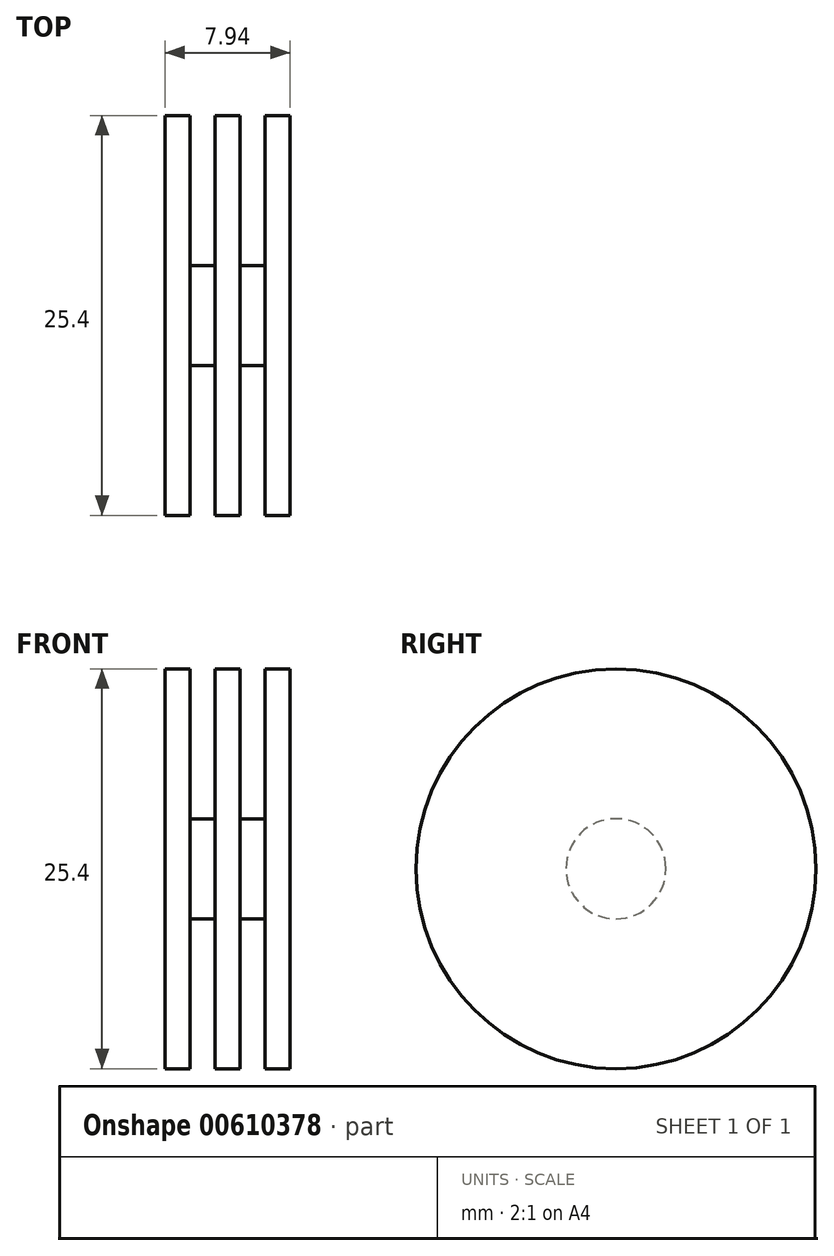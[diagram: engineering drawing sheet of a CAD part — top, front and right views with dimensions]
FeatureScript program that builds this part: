
annotation { "Feature Type Name" : "Feature", "Feature Type Description" : "" }
export const myFeature = defineFeature(function(context is Context, id is Id, definition is map)
    precondition{}
    {
        {
            var Q0;
            Q0=qCreatedBy(makeId("Right.planeOp"),FACE);
            var sketch = newSketch(context, id + "F0", { "sketchPlane" : qUnion([Q0])});
            skCircle(sketch, "E0", {"center": v(0, 0) * mm, "radius": 12.7 * mm});
            skSolve(sketch);
        }
        {
            var Q0;
            Q0=makeQuery(id+"F0.imprint","IMPRINT",FACE,{"disambiguationData":[TD([[makeQuery(id+"F0.imprint","IMPRINT",EDGE,{"derivedFrom":sQuery(id+"F0.wireOp",EDGE,"E0")}),1.0]])]});
            extrude(context, id + "F1", {"entities" : qUnion([Q0]), "oppositeDirection" : true, "depth" : 1.59 * mm, "offsetDistance" : 25.4 * mm});
        }
        {
            var Q0;
            Q0=makeQuery(id+"F1.opExtrude","CAP_FACE",FACE,{"disambiguationData":[OSD([sQuery(id+"F0.wireOp",EDGE,"E0")])],"isStart":true});
            var sketch = newSketch(context, id + "F2", { "sketchPlane" : qUnion([Q0])});
            skCircle(sketch, "E1", {"center": v(0, 0) * mm, "radius": 3.18 * mm});
            skSolve(sketch);
        }
        {
            var Q0;
            Q0=makeQuery(id+"F2.imprint","IMPRINT",FACE,{"disambiguationData":[TD([[makeQuery(id+"F2.imprint","IMPRINT",EDGE,{"derivedFrom":sQuery(id+"F2.wireOp",EDGE,"E1")}),1.0]])]});
            extrude(context, id + "F3", {"entities" : qUnion([Q0]), "operationType" : NewBodyOperationType.ADD, "depth" : 1.59 * mm, "offsetDistance" : 25.4 * mm});
        }
        {
            var Q0;
            Q0=makeQuery(id+"F3.opExtrude","CAP_FACE",FACE,{"disambiguationData":[OSD([sQuery(id+"F2.wireOp",EDGE,"E1")])],"isStart":false});
            var sketch = newSketch(context, id + "F4", { "sketchPlane" : qUnion([Q0])});
            skCircle(sketch, "E2.0.0", {"center": v(0, 0) * mm, "radius": 12.7 * mm});
            skSolve(sketch);
        }
        {
            var Q0;
            Q0=makeQuery(id+"F4.imprint","IMPRINT",FACE,{"disambiguationData":[TD([[makeQuery(id+"F4.imprint","IMPRINT",EDGE,{"derivedFrom":sQuery(id+"F4.wireOp",EDGE,"E2.0.0")}),1.0]])]});
            var Q1;
            Q1=makeQuery(id+"F4.imprint","IMPRINT",FACE,{"disambiguationData":[TD([[makeQuery(id+"F4.imprint","IMPRINT",EDGE,{"derivedFrom":makeQuery(id+"F3.opExtrude","CAP_EDGE",EDGE,{"disambiguationData":[OSD([sQuery(id+"F2.wireOp",EDGE,"E1")])],"isStart":false})}),1.0]])]});
            extrude(context, id + "F5", {"entities" : qUnion([Q0, Q1]), "depth" : 1.59 * mm, "offsetDistance" : 25.4 * mm});
        }
        {
            var Q0;
            Q0=makeQuery(id+"F5.opExtrude","CAP_FACE",FACE,{"disambiguationData":[OSD([sQuery(id+"F4.wireOp",EDGE,"E2.0.0")])],"isStart":false});
            var sketch = newSketch(context, id + "F6", { "sketchPlane" : qUnion([Q0])});
            skCircle(sketch, "E3.0.0", {"center": v(0, 0) * mm, "radius": 3.18 * mm});
            skSolve(sketch);
        }
        {
            var Q0;
            Q0=makeQuery(id+"F6.imprint","IMPRINT",FACE,{"disambiguationData":[TD([[makeQuery(id+"F6.imprint","IMPRINT",EDGE,{"derivedFrom":sQuery(id+"F6.wireOp",EDGE,"E3.0.0")}),1.0]])]});
            extrude(context, id + "F7", {"entities" : qUnion([Q0]), "operationType" : NewBodyOperationType.ADD, "depth" : 1.59 * mm, "offsetDistance" : 25.4 * mm});
        }
        {
            var Q0;
            Q0=makeQuery(id+"F7.opExtrude","CAP_FACE",FACE,{"disambiguationData":[OSD([sQuery(id+"F6.wireOp",EDGE,"E3.0.0")])],"isStart":false});
            var sketch = newSketch(context, id + "F8", { "sketchPlane" : qUnion([Q0])});
            skCircle(sketch, "E4.0.0", {"center": v(0, 0) * mm, "radius": 12.7 * mm});
            skSolve(sketch);
        }
        {
            var Q0;
            Q0=makeQuery(id+"F8.imprint","IMPRINT",FACE,{"disambiguationData":[TD([[makeQuery(id+"F8.imprint","IMPRINT",EDGE,{"derivedFrom":makeQuery(id+"F7.opExtrude","CAP_EDGE",EDGE,{"disambiguationData":[OSD([sQuery(id+"F6.wireOp",EDGE,"E3.0.0")])],"isStart":false})}),1.0]])]});
            var Q1;
            Q1=makeQuery(id+"F8.imprint","IMPRINT",FACE,{"disambiguationData":[TD([[makeQuery(id+"F8.imprint","IMPRINT",EDGE,{"derivedFrom":sQuery(id+"F8.wireOp",EDGE,"E4.0.0")}),1.0]])]});
            extrude(context, id + "F9", {"entities" : qUnion([Q0, Q1]), "operationType" : NewBodyOperationType.ADD, "depth" : 1.59 * mm, "offsetDistance" : 25.4 * mm});
        }
    });
